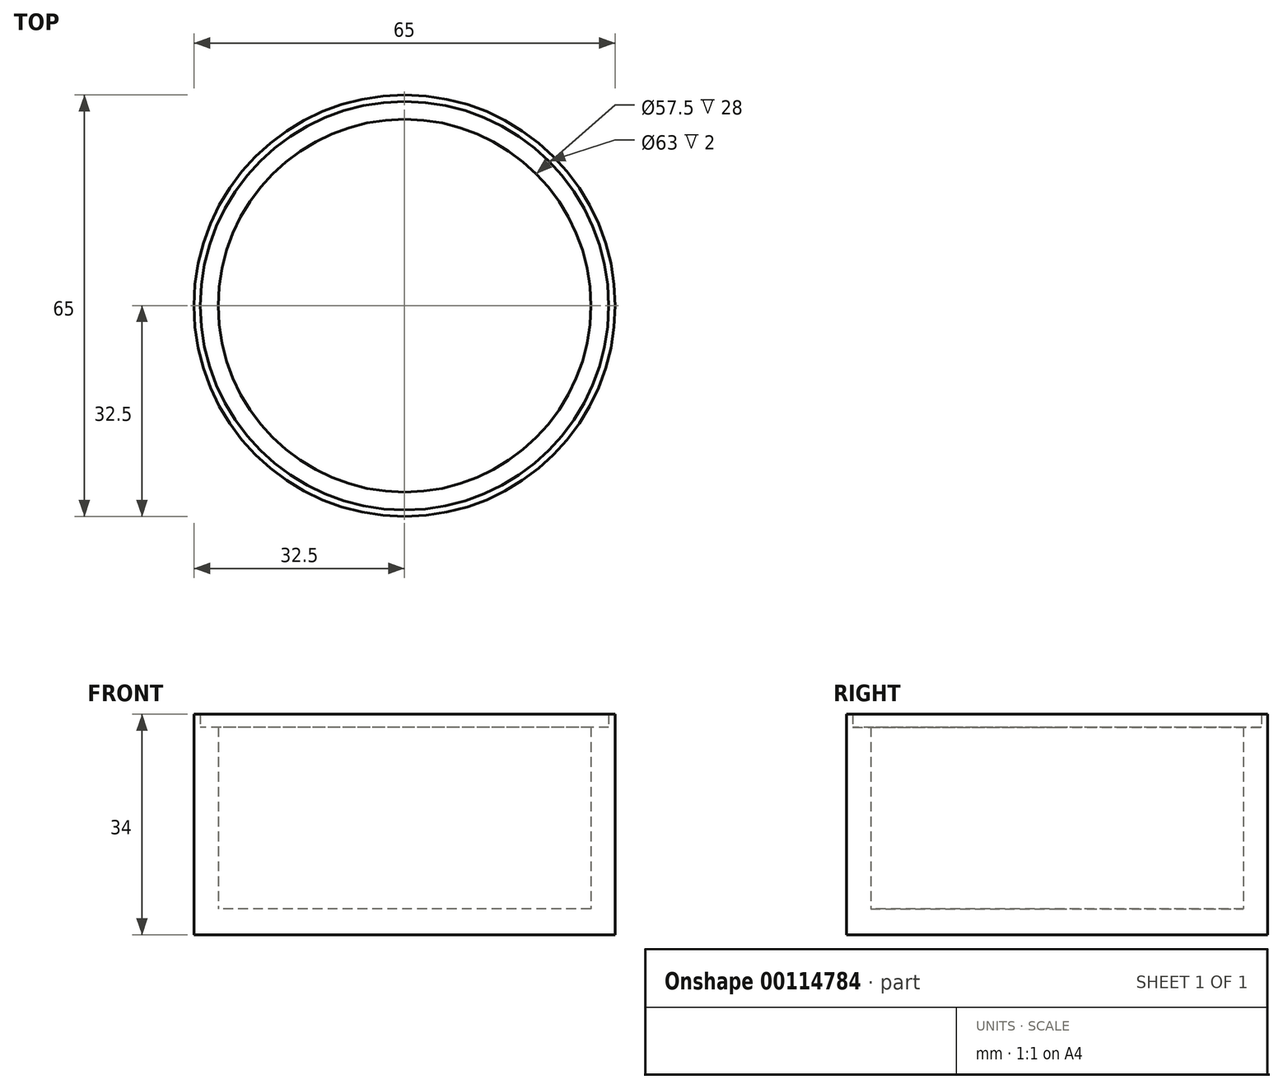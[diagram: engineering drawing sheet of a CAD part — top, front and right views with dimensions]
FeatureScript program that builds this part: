
annotation { "Feature Type Name" : "Feature", "Feature Type Description" : "" }
export const myFeature = defineFeature(function(context is Context, id is Id, definition is map)
    precondition{}
    {
        {
            var Q0;
            Q0=qCreatedBy(makeId("Top.planeOp"),FACE);
            var sketch = newSketch(context, id + "F0", { "sketchPlane" : qUnion([Q0])});
            skCircle(sketch, "E0", {"center": v(0, 0) * mm, "radius": 28.75 * mm});
            skCircle(sketch, "E1", {"center": v(0, 0) * mm, "radius": 31.5 * mm});
            skCircle(sketch, "E2", {"center": v(0, 0) * mm, "radius": 32.5 * mm});
            skSolve(sketch);
        }
        {
            var Q0;
            Q0=makeQuery(id+"F0.imprint","IMPRINT",FACE,{"disambiguationData":[TD([[makeQuery(id+"F0.imprint","IMPRINT",EDGE,{"derivedFrom":sQuery(id+"F0.wireOp",EDGE,"E0")}),-1.0]])]});
            extrude(context, id + "F1", {"entities" : qUnion([Q0]), "depth" : 28 * mm});
        }
        {
            var Q0;
            Q0=makeQuery(id+"F0.imprint","IMPRINT",FACE,{"disambiguationData":[TD([[makeQuery(id+"F0.imprint","IMPRINT",EDGE,{"derivedFrom":sQuery(id+"F0.wireOp",EDGE,"E1")}),-1.0]])]});
            extrude(context, id + "F2", {"entities" : qUnion([Q0]), "operationType" : NewBodyOperationType.ADD, "depth" : 30 * mm});
        }
        {
            var Q0;
            Q0=makeQuery(id+"F0.imprint","IMPRINT",FACE,{"disambiguationData":[TD([[makeQuery(id+"F0.imprint","IMPRINT",EDGE,{"derivedFrom":sQuery(id+"F0.wireOp",EDGE,"E1")}),-1.0]])]});
            var Q1;
            Q1=makeQuery(id+"F0.imprint","IMPRINT",FACE,{"disambiguationData":[TD([[makeQuery(id+"F0.imprint","IMPRINT",EDGE,{"derivedFrom":sQuery(id+"F0.wireOp",EDGE,"E0")}),-1.0]])]});
            var Q2;
            Q2=makeQuery(id+"F0.imprint","IMPRINT",FACE,{"disambiguationData":[TD([[makeQuery(id+"F0.imprint","IMPRINT",EDGE,{"derivedFrom":sQuery(id+"F0.wireOp",EDGE,"E0")}),1.0]])]});
            extrude(context, id + "F3", {"entities" : qUnion([Q0, Q1, Q2]), "operationType" : NewBodyOperationType.ADD, "oppositeDirection" : true, "depth" : 4 * mm});
        }
    });
